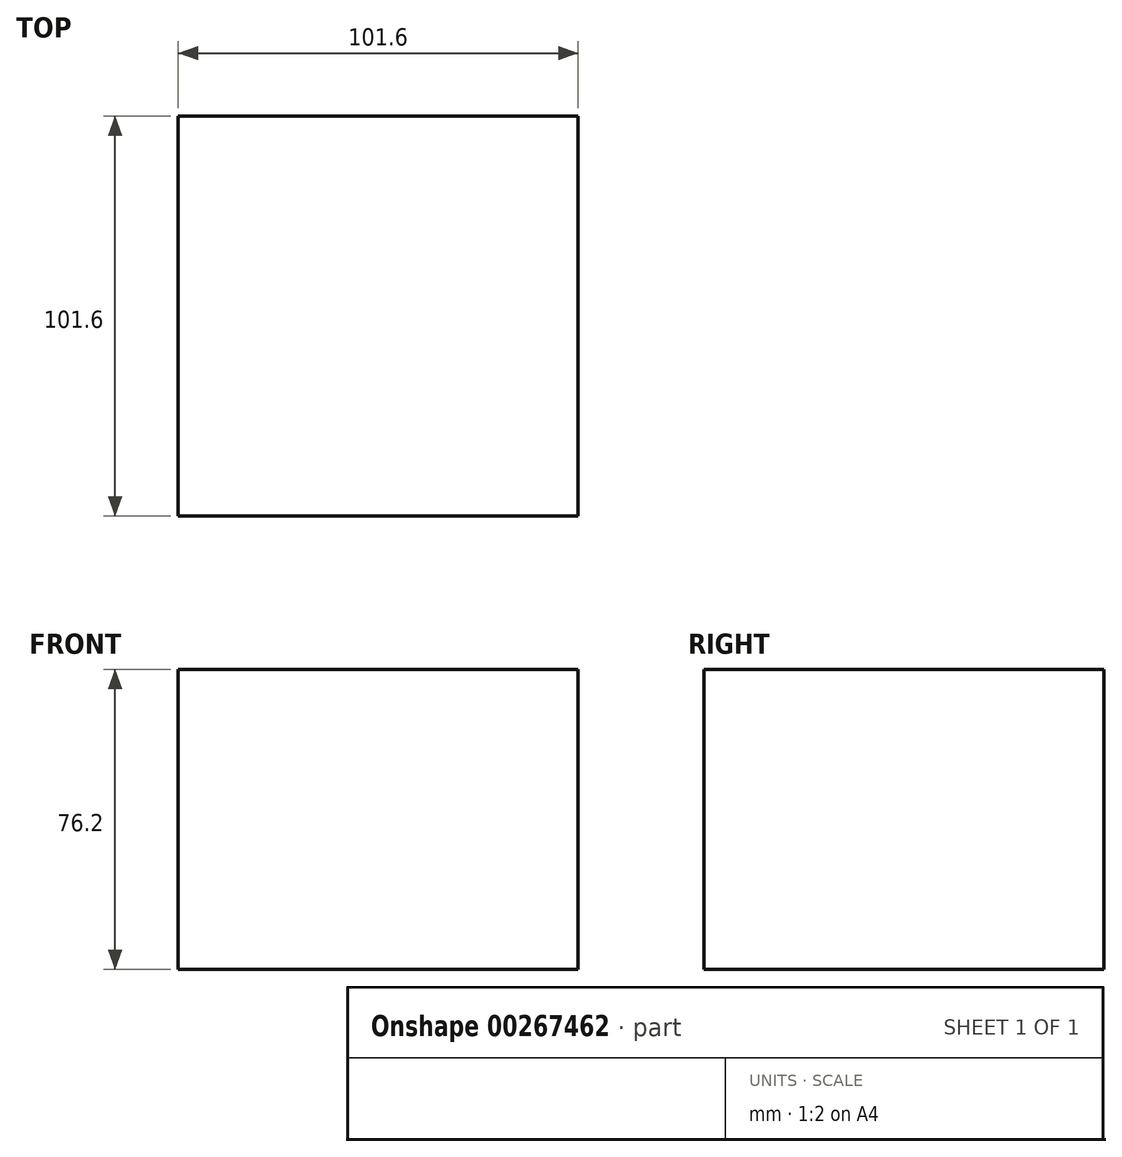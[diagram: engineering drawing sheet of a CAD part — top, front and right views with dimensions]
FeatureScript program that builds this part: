
annotation { "Feature Type Name" : "Feature", "Feature Type Description" : "" }
export const myFeature = defineFeature(function(context is Context, id is Id, definition is map)
    precondition{}
    {
        {
            var Q0;
            Q0=qCreatedBy(makeId("Top.planeOp"),FACE);
            var sketch = newSketch(context, id + "F0", { "sketchPlane" : qUnion([Q0])});
            skLineSegment(sketch, "E0.bottom", {"start": v(50.8, 50.8) * mm, "end": v(-50.8, 50.8) * mm});
            skLineSegment(sketch, "E0.top", {"start": v(50.8, -50.8) * mm, "end": v(-50.8, -50.8) * mm});
            skLineSegment(sketch, "E0.left", {"start": v(50.8, 50.8) * mm, "end": v(50.8, -50.8) * mm});
            skLineSegment(sketch, "E0.right", {"start": v(-50.8, 50.8) * mm, "end": v(-50.8, -50.8) * mm});
            skPoint(sketch, "E0.middle", {"position": v(0, 0) * mm});
            skSolve(sketch);
        }
        {
            var Q0;
            Q0 = qSketchRegion(id + "F0", true);
            extrude(context, id + "F1", {"entities" : qUnion([Q0]), "depth" : 76.2 * mm});
        }
    });
